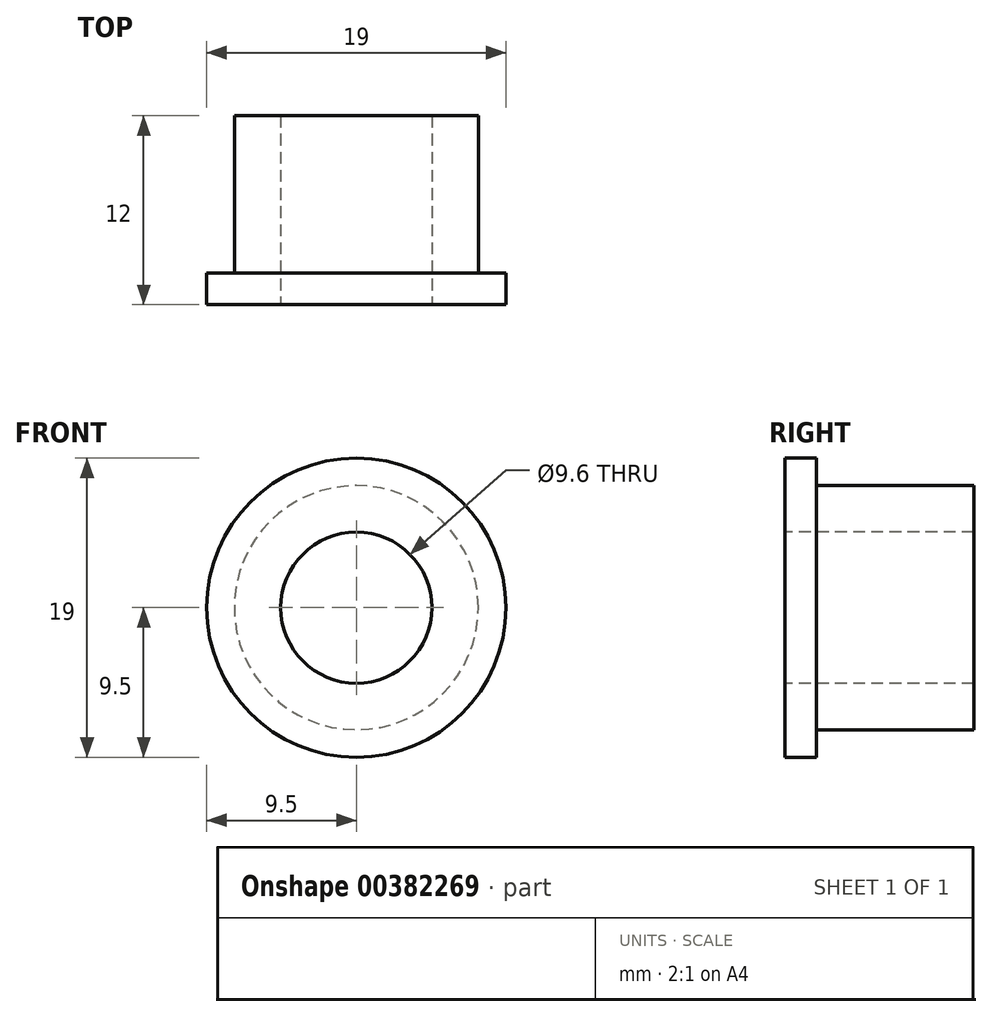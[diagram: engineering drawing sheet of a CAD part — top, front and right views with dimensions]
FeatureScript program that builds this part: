
annotation { "Feature Type Name" : "Feature", "Feature Type Description" : "" }
export const myFeature = defineFeature(function(context is Context, id is Id, definition is map)
    precondition{}
    {
        {
            var Q0;
            Q0=qCreatedBy(makeId("Front.planeOp"),FACE);
            var sketch = newSketch(context, id + "F0", { "sketchPlane" : qUnion([Q0])});
            skCircle(sketch, "E0", {"center": v(0, 0) * mm, "radius": 9.5 * mm});
            skCircle(sketch, "E1", {"center": v(0, 0) * mm, "radius": 4.8 * mm});
            skSolve(sketch);
        }
        {
            var Q0;
            Q0 = qSketchRegion(id + "F0", true);
            extrude(context, id + "F1", {"entities" : qUnion([Q0]), "oppositeDirection" : true, "offsetDistance" : 25 * mm, "depth" : 12 * mm});
        }
        {
            var Q0;
            Q0=makeQuery(id+"F1.opExtrude","CAP_FACE",FACE,{"disambiguationData":[OSD([sQuery(id+"F0.wireOp",EDGE,"E0"),sQuery(id+"F0.wireOp",EDGE,"E1")])],"isStart":false});
            var sketch = newSketch(context, id + "F2", { "sketchPlane" : qUnion([Q0])});
            skCircle(sketch, "E2", {"center": v(0, 0) * mm, "radius": 7.75 * mm});
            skSolve(sketch);
        }
        {
            var Q0;
            Q0=makeQuery(id+"F2.imprint","IMPRINT",FACE,{"disambiguationData":[TD([[makeQuery(id+"F2.imprint","IMPRINT",EDGE,{"derivedFrom":sQuery(id+"F2.wireOp",EDGE,"E2")}),-1.0]])]});
            extrude(context, id + "F3", {"entities" : qUnion([Q0]), "operationType" : NewBodyOperationType.REMOVE, "oppositeDirection" : true, "offsetDistance" : 25 * mm, "depth" : 10 * mm});
        }
    });
